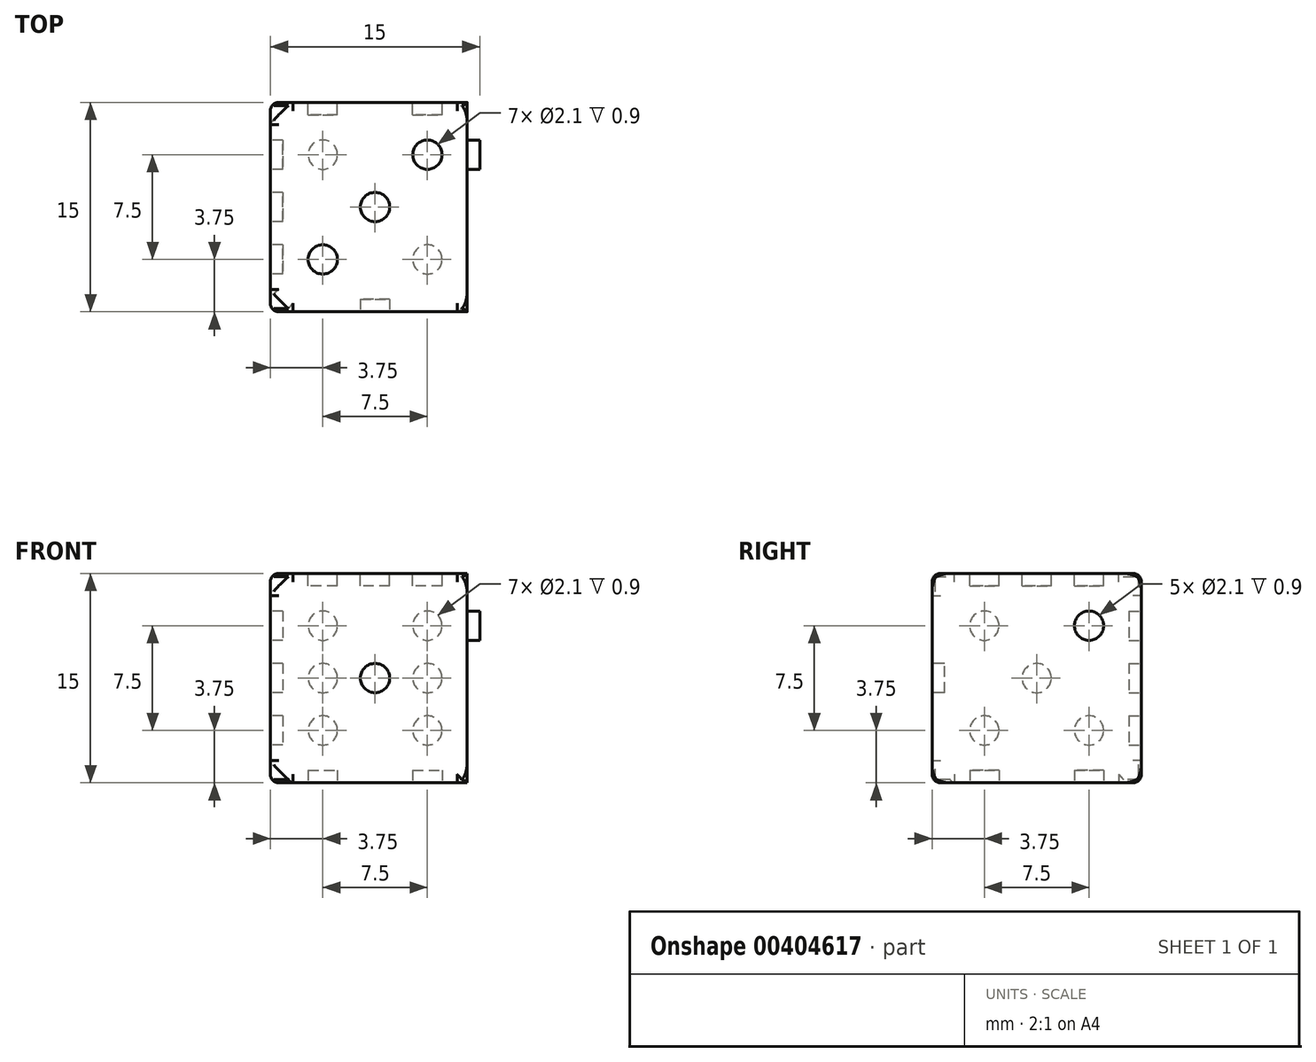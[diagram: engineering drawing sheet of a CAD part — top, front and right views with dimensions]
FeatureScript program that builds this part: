
annotation { "Feature Type Name" : "Feature", "Feature Type Description" : "" }
export const myFeature = defineFeature(function(context is Context, id is Id, definition is map)
    precondition{}
    {
        {
            var Q0;
            Q0=qCreatedBy(makeId("Front.planeOp"),FACE);
            var sketch = newSketch(context, id + "F0", { "sketchPlane" : qUnion([Q0])});
            skLineSegment(sketch, "E0.bottom", {"start": v(0, 25) * mm, "end": v(25, 25) * mm});
            skLineSegment(sketch, "E0.top", {"start": v(0, 0) * mm, "end": v(25, 0) * mm});
            skLineSegment(sketch, "E0.left", {"start": v(0, 25) * mm, "end": v(0, 0) * mm});
            skLineSegment(sketch, "E0.right", {"start": v(25, 25) * mm, "end": v(25, 0) * mm});
            skSolve(sketch);
        }
        {
            var Q0;
            Q0=makeQuery(id+"F0.imprint","IMPRINT",FACE,{"disambiguationData":[TD([[makeQuery(id+"F0.imprint","IMPRINT",EDGE,{"derivedFrom":sQuery(id+"F0.wireOp",EDGE,"E0.bottom")}),-1.0]])]});
            extrude(context, id + "F1", {"entities" : qUnion([Q0]), "oppositeDirection" : true, "depth" : 25 * mm});
        }
        {
            var Q0;
            Q0=makeQuery(id+"F1.opExtrude","CAP_FACE",FACE,{"disambiguationData":[OSD([sQuery(id+"F0.wireOp",EDGE,"E0.bottom"),sQuery(id+"F0.wireOp",EDGE,"E0.top"),sQuery(id+"F0.wireOp",EDGE,"E0.left"),sQuery(id+"F0.wireOp",EDGE,"E0.right")])],"isStart":true});
            var sketch = newSketch(context, id + "F2", { "sketchPlane" : qUnion([Q0])});
            skLineSegment(sketch, "E1", {"start": v(0, 12.5) * mm, "end": v(25, 12.5) * mm, "construction": true});
            skLineSegment(sketch, "E2", {"start": v(12.5, 25) * mm, "end": v(12.5, 0) * mm, "construction": true});
            skCircle(sketch, "E3", {"center": v(12.5, 12.5) * mm, "radius": 1.75 * mm});
            skSolve(sketch);
        }
        {
            var Q0;
            Q0 = qSketchRegion(id + "F2", true);
            extrude(context, id + "F3", {"entities" : qUnion([Q0]), "operationType" : NewBodyOperationType.REMOVE, "oppositeDirection" : true, "depth" : 1.5 * mm});
        }
        {
            var Q0;
            Q0=makeQuery(id+"F1.opExtrude","SWEPT_FACE",FACE,{"disambiguationData":[OSD([sQuery(id+"F0.wireOp",EDGE,"E0.right")])]});
            var sketch = newSketch(context, id + "F4", { "sketchPlane" : qUnion([Q0])});
            skLineSegment(sketch, "E4", {"start": v(0, 0) * mm, "end": v(25, 25) * mm, "construction": true});
            skCircle(sketch, "E5", {"center": v(6.25, 6.25) * mm, "radius": 1.75 * mm});
            skLineSegment(sketch, "E6", {"start": v(0, 25) * mm, "end": v(25, 0) * mm, "construction": true});
            skCircle(sketch, "E7.MirrorC", {"center": v(18.75, 18.75) * mm, "radius": 1.75 * mm});
            skLineSegment(sketch, "E8", {"start": v(12.5, 12.5) * mm, "end": v(12.5, 0) * mm, "construction": true});
            skLineSegment(sketch, "E9", {"start": v(12.5, 0) * mm, "end": v(6.25, 6.25) * mm, "construction": true});
            skSolve(sketch);
        }
        {
            var Q0;
            Q0=makeQuery(id+"F4.imprint","IMPRINT",FACE,{"disambiguationData":[TD([[makeQuery(id+"F4.imprint","IMPRINT",EDGE,{"derivedFrom":sQuery(id+"F4.wireOp",EDGE,"E7.MirrorC")}),-1.0]])]});
            var Q1;
            Q1=makeQuery(id+"F4.imprint","IMPRINT",FACE,{"disambiguationData":[TD([[makeQuery(id+"F4.imprint","IMPRINT",EDGE,{"derivedFrom":sQuery(id+"F4.wireOp",EDGE,"E5")}),1.0]])]});
            var Q2;
            Q2=sQuery(id+"F4.wireOp",EDGE,"E5");
            var Q3;
            Q3=sQuery(id+"F4.wireOp",EDGE,"E7.MirrorC");
            extrude(context, id + "F5", {"entities" : qUnion([Q0, Q1]), "operationType" : NewBodyOperationType.REMOVE, "surfaceEntities" : qUnion([Q2, Q3]), "oppositeDirection" : true, "depth" : 1.5 * mm});
        }
        {
            var Q0;
            Q0=makeQuery(id+"F1.opExtrude","CAP_FACE",FACE,{"disambiguationData":[OSD([sQuery(id+"F0.wireOp",EDGE,"E0.bottom"),sQuery(id+"F0.wireOp",EDGE,"E0.top"),sQuery(id+"F0.wireOp",EDGE,"E0.left"),sQuery(id+"F0.wireOp",EDGE,"E0.right")])],"isStart":false});
            var sketch = newSketch(context, id + "F6", { "sketchPlane" : qUnion([Q0])});
            skLineSegment(sketch, "E10", {"start": v(-12.5, 25) * mm, "end": v(-12.5, 0) * mm, "construction": true});
            skLineSegment(sketch, "E11", {"start": v(-25, 25) * mm, "end": v(0, 0) * mm, "construction": true});
            skLineSegment(sketch, "E12", {"start": v(0, 25) * mm, "end": v(-25, 0) * mm, "construction": true});
            skLineSegment(sketch, "E13", {"start": v(0, 12.5) * mm, "end": v(-25, 12.5) * mm, "construction": true});
            skLineSegment(sketch, "E14", {"start": v(-25, 12.5) * mm, "end": v(-18.75, 18.75) * mm, "construction": true});
            skLineSegment(sketch, "E15", {"start": v(-18.75, 25) * mm, "end": v(-18.75, 0) * mm, "construction": true});
            skLineSegment(sketch, "E16", {"start": v(0, 12.5) * mm, "end": v(-6.25, 18.75) * mm, "construction": true});
            skLineSegment(sketch, "E17", {"start": v(-6.25, 25) * mm, "end": v(-6.25, 0) * mm, "construction": true});
            skCircle(sketch, "E18", {"center": v(-18.75, 18.75) * mm, "radius": 1.75 * mm});
            skCircle(sketch, "E19", {"center": v(-18.75, 12.5) * mm, "radius": 1.75 * mm});
            skCircle(sketch, "E20", {"center": v(-18.75, 6.25) * mm, "radius": 1.75 * mm});
            skCircle(sketch, "E21", {"center": v(-6.25, 18.75) * mm, "radius": 1.75 * mm});
            skCircle(sketch, "E22", {"center": v(-6.25, 12.5) * mm, "radius": 1.75 * mm});
            skCircle(sketch, "E23", {"center": v(-6.25, 6.25) * mm, "radius": 1.75 * mm});
            skSolve(sketch);
        }
        {
            var Q0;
            Q0 = qSketchRegion(id + "F6", true);
            extrude(context, id + "F7", {"entities" : qUnion([Q0]), "operationType" : NewBodyOperationType.REMOVE, "oppositeDirection" : true, "depth" : 1.5 * mm});
        }
        {
            var Q0;
            Q0=makeQuery(id+"F1.opExtrude","SWEPT_FACE",FACE,{"disambiguationData":[OSD([sQuery(id+"F0.wireOp",EDGE,"E0.left")])]});
            var sketch = newSketch(context, id + "F8", { "sketchPlane" : qUnion([Q0])});
            skLineSegment(sketch, "E24", {"start": v(-12.5, 25) * mm, "end": v(-12.5, 0) * mm, "construction": true});
            skLineSegment(sketch, "E25", {"start": v(0, 12.5) * mm, "end": v(-25, 12.5) * mm, "construction": true});
            skLineSegment(sketch, "E26", {"start": v(-25, 12.5) * mm, "end": v(-12.5, 25) * mm, "construction": true});
            skLineSegment(sketch, "E27", {"start": v(-12.5, 12.5) * mm, "end": v(-25, 25) * mm, "construction": true});
            skLineSegment(sketch, "E28", {"start": v(-18.75, 18.75) * mm, "end": v(-18.75, 12.5) * mm, "construction": true});
            skLineSegment(sketch, "E29", {"start": v(-18.75, 18.75) * mm, "end": v(-12.5, 18.75) * mm, "construction": true});
            skCircle(sketch, "E30", {"center": v(-18.75, 18.75) * mm, "radius": 1.75 * mm});
            skCircle(sketch, "E31.MirrorC", {"center": v(-18.75, 6.25) * mm, "radius": 1.75 * mm});
            skLineSegment(sketch, "E32.MirrorCS", {"start": v(-12.5, 0) * mm, "end": v(-12.5, 25) * mm, "construction": true});
            skCircle(sketch, "E33.MirrorC", {"center": v(-6.25, 18.75) * mm, "radius": 1.75 * mm});
            skCircle(sketch, "E34.MirrorC", {"center": v(-6.25, 6.25) * mm, "radius": 1.75 * mm});
            skCircle(sketch, "E35", {"center": v(-12.5, 12.5) * mm, "radius": 1.75 * mm});
            skSolve(sketch);
        }
        {
            var Q0;
            Q0 = qSketchRegion(id + "F8", true);
            extrude(context, id + "F9", {"entities" : qUnion([Q0]), "operationType" : NewBodyOperationType.REMOVE, "oppositeDirection" : true, "depth" : 1.5 * mm});
        }
        {
            var Q0;
            Q0=makeQuery(id+"F1.opExtrude","SWEPT_FACE",FACE,{"disambiguationData":[OSD([sQuery(id+"F0.wireOp",EDGE,"E0.bottom")])]});
            var sketch = newSketch(context, id + "F10", { "sketchPlane" : qUnion([Q0])});
            skLineSegment(sketch, "E36", {"start": v(0, 0) * mm, "end": v(25, 25) * mm, "construction": true});
            skLineSegment(sketch, "E37", {"start": v(25, 25) * mm, "end": v(0, 25) * mm, "construction": true});
            skLineSegment(sketch, "E38", {"start": v(0, 25) * mm, "end": v(25, 0) * mm, "construction": true});
            skLineSegment(sketch, "E39", {"start": v(12.5, 12.5) * mm, "end": v(0, 12.5) * mm, "construction": true});
            skLineSegment(sketch, "E40", {"start": v(0, 12.5) * mm, "end": v(6.25, 6.25) * mm, "construction": true});
            skCircle(sketch, "E41", {"center": v(6.25, 6.25) * mm, "radius": 1.75 * mm});
            skCircle(sketch, "E42.MirrorC", {"center": v(18.75, 18.75) * mm, "radius": 1.75 * mm});
            skCircle(sketch, "E43", {"center": v(12.5, 12.5) * mm, "radius": 1.75 * mm});
            skSolve(sketch);
        }
        {
            var Q0;
            Q0 = qSketchRegion(id + "F10", true);
            extrude(context, id + "F11", {"entities" : qUnion([Q0]), "operationType" : NewBodyOperationType.REMOVE, "oppositeDirection" : true, "depth" : 1.5 * mm});
        }
        {
            var Q0;
            Q0=makeQuery(id+"F1.opExtrude","SWEPT_FACE",FACE,{"disambiguationData":[OSD([sQuery(id+"F0.wireOp",EDGE,"E0.top")])]});
            var sketch = newSketch(context, id + "F12", { "sketchPlane" : qUnion([Q0])});
            skLineSegment(sketch, "E44", {"start": v(12.5, 0) * mm, "end": v(12.5, -25) * mm, "construction": true});
            skLineSegment(sketch, "E45", {"start": v(12.5, -25) * mm, "end": v(0, -12.5) * mm, "construction": true});
            skLineSegment(sketch, "E46", {"start": v(0, -12.5) * mm, "end": v(25, -12.5) * mm, "construction": true});
            skLineSegment(sketch, "E47", {"start": v(0, -25) * mm, "end": v(6.25, -18.75) * mm, "construction": true});
            skLineSegment(sketch, "E48", {"start": v(6.25, -25) * mm, "end": v(6.25, 0) * mm, "construction": true});
            skCircle(sketch, "E49", {"center": v(6.25, -18.75) * mm, "radius": 1.75 * mm});
            skCircle(sketch, "E50.MirrorC", {"center": v(6.25, -6.25) * mm, "radius": 1.75 * mm});
            skCircle(sketch, "E51.MirrorC", {"center": v(18.75, -18.75) * mm, "radius": 1.75 * mm});
            skCircle(sketch, "E52.MirrorC", {"center": v(18.75, -6.25) * mm, "radius": 1.75 * mm});
            skSolve(sketch);
        }
        {
            var Q0;
            Q0 = qSketchRegion(id + "F12", true);
            extrude(context, id + "F13", {"entities" : qUnion([Q0]), "operationType" : NewBodyOperationType.REMOVE, "oppositeDirection" : true, "depth" : 1.5 * mm});
        }
        {
            var Q0;
            Q0=makeQuery(id+"F1.opExtrude","SWEPT_BODY",BODY,{"disambiguationData":[OSD([sQuery(id+"F0.wireOp",EDGE,"E0.bottom"),sQuery(id+"F0.wireOp",EDGE,"E0.top"),sQuery(id+"F0.wireOp",EDGE,"E0.left"),sQuery(id+"F0.wireOp",EDGE,"E0.right")])]});
            transform(context, id + "F14", {"entities" : qUnion([Q0]), "transformType" : TransformType.TRANSLATION_3D, "dx" : (-25 / 2) * mm, "dy" : (-25 / 2) * mm, "dz" : (-25 / 2) * mm, "makeCopy" : false});
        }
        {
            var Q0;
            Q0=qCreatedBy(makeId("Front.planeOp"),FACE);
            var sketch = newSketch(context, id + "F15", { "sketchPlane" : qUnion([Q0])});
            skArc(sketch, "E53", {"start": v(20, 0) * mm, "mid": v(0, 20) * mm, "end": v(-20, 0) * mm});
            skLineSegment(sketch, "E54", {"start": v(20, 0) * mm, "end": v(-20, 0) * mm});
            skSolve(sketch);
        }
        {
            var Q0;
            Q0=makeQuery(id+"F15.imprint","IMPRINT",FACE,{"disambiguationData":[TD([[makeQuery(id+"F15.imprint","IMPRINT",EDGE,{"derivedFrom":sQuery(id+"F15.wireOp",EDGE,"E53")}),1.0]])]});
            var Q1;
            Q1=sQuery(id+"F15.wireOp",EDGE,"E54");
            revolve(context, id + "F16", {"entities" : qUnion([Q0]), "axis" : qUnion([Q1]), "revolveType" : RevolveType.FULL});
        }
        {
            var Q0;
            Q0=makeQuery(id+"F1.opExtrude","CAP_EDGE",EDGE,{"disambiguationData":[OSD([sQuery(id+"F0.wireOp",EDGE,"E0.left")])],"isStart":false});
            var Q1;
            Q1=makeQuery(id+"F1.opExtrude","CAP_EDGE",EDGE,{"disambiguationData":[OSD([sQuery(id+"F0.wireOp",EDGE,"E0.top")])],"isStart":false});
            var Q2;
            Q2=makeQuery(id+"F1.opExtrude","SWEPT_EDGE",EDGE,{"disambiguationData":[OSD([sQuery(id+"F0.wireOp",EDGE,"E0.top"),sQuery(id+"F0.wireOp",EDGE,"E0.left")])]});
            var Q3;
            Q3=makeQuery(id+"F1.opExtrude","CAP_EDGE",EDGE,{"disambiguationData":[OSD([sQuery(id+"F0.wireOp",EDGE,"E0.left")])],"isStart":true});
            var Q4;
            Q4=makeQuery(id+"F1.opExtrude","SWEPT_EDGE",EDGE,{"disambiguationData":[OSD([sQuery(id+"F0.wireOp",EDGE,"E0.bottom"),sQuery(id+"F0.wireOp",EDGE,"E0.left")])]});
            var Q5;
            Q5=makeQuery(id+"F1.opExtrude","CAP_EDGE",EDGE,{"disambiguationData":[OSD([sQuery(id+"F0.wireOp",EDGE,"E0.right")])],"isStart":false});
            var Q6;
            Q6=makeQuery(id+"F1.opExtrude","SWEPT_EDGE",EDGE,{"disambiguationData":[OSD([sQuery(id+"F0.wireOp",EDGE,"E0.top"),sQuery(id+"F0.wireOp",EDGE,"E0.right")])]});
            var Q7;
            Q7=makeQuery(id+"F1.opExtrude","CAP_EDGE",EDGE,{"disambiguationData":[OSD([sQuery(id+"F0.wireOp",EDGE,"E0.top")])],"isStart":true});
            var Q8;
            Q8=makeQuery(id+"F1.opExtrude","CAP_EDGE",EDGE,{"disambiguationData":[OSD([sQuery(id+"F0.wireOp",EDGE,"E0.bottom")])],"isStart":false});
            var Q9;
            Q9=makeQuery(id+"F1.opExtrude","CAP_EDGE",EDGE,{"disambiguationData":[OSD([sQuery(id+"F0.wireOp",EDGE,"E0.bottom")])],"isStart":true});
            var Q10;
            Q10=makeQuery(id+"F1.opExtrude","CAP_EDGE",EDGE,{"disambiguationData":[OSD([sQuery(id+"F0.wireOp",EDGE,"E0.right")])],"isStart":true});
            var Q11;
            Q11=makeQuery(id+"F1.opExtrude","SWEPT_EDGE",EDGE,{"disambiguationData":[OSD([sQuery(id+"F0.wireOp",EDGE,"E0.bottom"),sQuery(id+"F0.wireOp",EDGE,"E0.right")])]});
            fillet(context, id + "F17", {"entities" : qUnion([Q0, Q1, Q2, Q3, Q4, Q5, Q6, Q7, Q8, Q9, Q10, Q11]), "radius" : 1 * mm, "tangentPropagation" : true, "allowEdgeOverflow" : false});
        }
        {
            var Q0;
            Q0=makeQuery(id+"F16.opRevolve","SWEPT_BODY",BODY,{"disambiguationData":[OSD([sQuery(id+"F15.wireOp",EDGE,"E53"),sQuery(id+"F15.wireOp",EDGE,"E54")])]});
            var Q1;
            Q1=makeQuery(id+"F1.opExtrude","SWEPT_BODY",BODY,{"disambiguationData":[OSD([sQuery(id+"F0.wireOp",EDGE,"E0.bottom"),sQuery(id+"F0.wireOp",EDGE,"E0.top"),sQuery(id+"F0.wireOp",EDGE,"E0.left"),sQuery(id+"F0.wireOp",EDGE,"E0.right")])]});
            booleanBodies(context, id + "F18", {"operationType" : BooleanOperationType.INTERSECTION, "tools" : qUnion([Q0, Q1])});
        }
        {
            var Q0;
            {var subQ0=sQuery(id+"F0.wireOp",EDGE,"E0.right");var subQ1=sQuery(id+"F0.wireOp",EDGE,"E0.bottom");Q0=makeQuery(id+"F18.opBoolean","SPLIT",FACE,{"disambiguationData":[TD([makeQuery(id+"F1.opExtrude","SWEPT_FACE",FACE,{"disambiguationData":[OSD([subQ1])]}),makeQuery(id+"F1.opExtrude","CAP_FACE",FACE,{"disambiguationData":[OSD([subQ1,sQuery(id+"F0.wireOp",EDGE,"E0.top"),sQuery(id+"F0.wireOp",EDGE,"E0.left"),subQ0])],"isStart":true}),makeQuery(id+"F1.opExtrude","SWEPT_FACE",FACE,{"disambiguationData":[OSD([subQ0])]}),makeQuery(id+"F17.opFillet","BLEND_FACE",FACE,{"disambiguationData":[OSD([subQ1,subQ0]),TDD([makeQuery(id+"F1.opExtrude","SWEPT_EDGE",EDGE,{"disambiguationData":[OSD([subQ1,subQ0])]})])]}),makeQuery(id+"F17.opFillet","BLEND_FACE",FACE,{"disambiguationData":[OSD([subQ1]),TDD([makeQuery(id+"F1.opExtrude","CAP_EDGE",EDGE,{"disambiguationData":[OSD([subQ1])],"isStart":true})])]}),makeQuery(id+"F17.opFillet","BLEND_FACE",FACE,{"disambiguationData":[OSD([subQ0]),TDD([makeQuery(id+"F1.opExtrude","CAP_EDGE",EDGE,{"disambiguationData":[OSD([subQ0])],"isStart":true})])]})])],"derivedFrom":makeQuery(id+"F16.opRevolve","SWEPT_FACE",FACE,{"disambiguationData":[OSD([sQuery(id+"F15.wireOp",EDGE,"E53")])]})});}
            var Q1;
            {var subQ0=sQuery(id+"F0.wireOp",EDGE,"E0.left");var subQ1=sQuery(id+"F0.wireOp",EDGE,"E0.bottom");Q1=makeQuery(id+"F18.opBoolean","SPLIT",FACE,{"disambiguationData":[TD([makeQuery(id+"F1.opExtrude","SWEPT_FACE",FACE,{"disambiguationData":[OSD([subQ1])]}),makeQuery(id+"F1.opExtrude","CAP_FACE",FACE,{"disambiguationData":[OSD([subQ1,sQuery(id+"F0.wireOp",EDGE,"E0.top"),subQ0,sQuery(id+"F0.wireOp",EDGE,"E0.right")])],"isStart":true}),makeQuery(id+"F1.opExtrude","SWEPT_FACE",FACE,{"disambiguationData":[OSD([subQ0])]}),makeQuery(id+"F17.opFillet","BLEND_FACE",FACE,{"disambiguationData":[OSD([subQ1,subQ0]),TDD([makeQuery(id+"F1.opExtrude","SWEPT_EDGE",EDGE,{"disambiguationData":[OSD([subQ1,subQ0])]})])]}),makeQuery(id+"F17.opFillet","BLEND_FACE",FACE,{"disambiguationData":[OSD([subQ1]),TDD([makeQuery(id+"F1.opExtrude","CAP_EDGE",EDGE,{"disambiguationData":[OSD([subQ1])],"isStart":true})])]}),makeQuery(id+"F17.opFillet","BLEND_FACE",FACE,{"disambiguationData":[OSD([subQ0]),TDD([makeQuery(id+"F1.opExtrude","CAP_EDGE",EDGE,{"disambiguationData":[OSD([subQ0])],"isStart":true})])]})])],"derivedFrom":makeQuery(id+"F16.opRevolve","SWEPT_FACE",FACE,{"disambiguationData":[OSD([sQuery(id+"F15.wireOp",EDGE,"E53")])]})});}
            var Q2;
            {var subQ0=sQuery(id+"F0.wireOp",EDGE,"E0.right");var subQ1=sQuery(id+"F0.wireOp",EDGE,"E0.bottom");Q2=makeQuery(id+"F18.opBoolean","SPLIT",FACE,{"disambiguationData":[TD([makeQuery(id+"F1.opExtrude","SWEPT_FACE",FACE,{"disambiguationData":[OSD([subQ1])]}),makeQuery(id+"F1.opExtrude","CAP_FACE",FACE,{"disambiguationData":[OSD([subQ1,sQuery(id+"F0.wireOp",EDGE,"E0.top"),sQuery(id+"F0.wireOp",EDGE,"E0.left"),subQ0])],"isStart":false}),makeQuery(id+"F1.opExtrude","SWEPT_FACE",FACE,{"disambiguationData":[OSD([subQ0])]}),makeQuery(id+"F17.opFillet","BLEND_FACE",FACE,{"disambiguationData":[OSD([subQ1,subQ0]),TDD([makeQuery(id+"F1.opExtrude","SWEPT_EDGE",EDGE,{"disambiguationData":[OSD([subQ1,subQ0])]})])]}),makeQuery(id+"F17.opFillet","BLEND_FACE",FACE,{"disambiguationData":[OSD([subQ1]),TDD([makeQuery(id+"F1.opExtrude","CAP_EDGE",EDGE,{"disambiguationData":[OSD([subQ1])],"isStart":false})])]}),makeQuery(id+"F17.opFillet","BLEND_FACE",FACE,{"disambiguationData":[OSD([subQ0]),TDD([makeQuery(id+"F1.opExtrude","CAP_EDGE",EDGE,{"disambiguationData":[OSD([subQ0])],"isStart":false})])]})])],"derivedFrom":makeQuery(id+"F16.opRevolve","SWEPT_FACE",FACE,{"disambiguationData":[OSD([sQuery(id+"F15.wireOp",EDGE,"E53")])]})});}
            var Q3;
            {var subQ0=sQuery(id+"F0.wireOp",EDGE,"E0.left");var subQ1=sQuery(id+"F0.wireOp",EDGE,"E0.bottom");Q3=makeQuery(id+"F18.opBoolean","SPLIT",FACE,{"disambiguationData":[TD([makeQuery(id+"F1.opExtrude","SWEPT_FACE",FACE,{"disambiguationData":[OSD([subQ1])]}),makeQuery(id+"F1.opExtrude","CAP_FACE",FACE,{"disambiguationData":[OSD([subQ1,sQuery(id+"F0.wireOp",EDGE,"E0.top"),subQ0,sQuery(id+"F0.wireOp",EDGE,"E0.right")])],"isStart":false}),makeQuery(id+"F1.opExtrude","SWEPT_FACE",FACE,{"disambiguationData":[OSD([subQ0])]}),makeQuery(id+"F17.opFillet","BLEND_FACE",FACE,{"disambiguationData":[OSD([subQ1,subQ0]),TDD([makeQuery(id+"F1.opExtrude","SWEPT_EDGE",EDGE,{"disambiguationData":[OSD([subQ1,subQ0])]})])]}),makeQuery(id+"F17.opFillet","BLEND_FACE",FACE,{"disambiguationData":[OSD([subQ1]),TDD([makeQuery(id+"F1.opExtrude","CAP_EDGE",EDGE,{"disambiguationData":[OSD([subQ1])],"isStart":false})])]}),makeQuery(id+"F17.opFillet","BLEND_FACE",FACE,{"disambiguationData":[OSD([subQ0]),TDD([makeQuery(id+"F1.opExtrude","CAP_EDGE",EDGE,{"disambiguationData":[OSD([subQ0])],"isStart":false})])]})])],"derivedFrom":makeQuery(id+"F16.opRevolve","SWEPT_FACE",FACE,{"disambiguationData":[OSD([sQuery(id+"F15.wireOp",EDGE,"E53")])]})});}
            var Q4;
            {var subQ0=sQuery(id+"F0.wireOp",EDGE,"E0.left");var subQ1=sQuery(id+"F0.wireOp",EDGE,"E0.top");Q4=makeQuery(id+"F18.opBoolean","SPLIT",FACE,{"disambiguationData":[TD([makeQuery(id+"F1.opExtrude","CAP_FACE",FACE,{"disambiguationData":[OSD([sQuery(id+"F0.wireOp",EDGE,"E0.bottom"),subQ1,subQ0,sQuery(id+"F0.wireOp",EDGE,"E0.right")])],"isStart":true}),makeQuery(id+"F1.opExtrude","SWEPT_FACE",FACE,{"disambiguationData":[OSD([subQ1])]}),makeQuery(id+"F1.opExtrude","SWEPT_FACE",FACE,{"disambiguationData":[OSD([subQ0])]}),makeQuery(id+"F17.opFillet","BLEND_FACE",FACE,{"disambiguationData":[OSD([subQ1,subQ0]),TDD([makeQuery(id+"F1.opExtrude","SWEPT_EDGE",EDGE,{"disambiguationData":[OSD([subQ1,subQ0])]})])]}),makeQuery(id+"F17.opFillet","BLEND_FACE",FACE,{"disambiguationData":[OSD([subQ1]),TDD([makeQuery(id+"F1.opExtrude","CAP_EDGE",EDGE,{"disambiguationData":[OSD([subQ1])],"isStart":true})])]}),makeQuery(id+"F17.opFillet","BLEND_FACE",FACE,{"disambiguationData":[OSD([subQ0]),TDD([makeQuery(id+"F1.opExtrude","CAP_EDGE",EDGE,{"disambiguationData":[OSD([subQ0])],"isStart":true})])]})])],"derivedFrom":makeQuery(id+"F16.opRevolve","SWEPT_FACE",FACE,{"disambiguationData":[OSD([sQuery(id+"F15.wireOp",EDGE,"E53")])]})});}
            var Q5;
            {var subQ0=sQuery(id+"F0.wireOp",EDGE,"E0.left");var subQ1=sQuery(id+"F0.wireOp",EDGE,"E0.top");Q5=makeQuery(id+"F18.opBoolean","SPLIT",FACE,{"disambiguationData":[TD([makeQuery(id+"F1.opExtrude","CAP_FACE",FACE,{"disambiguationData":[OSD([sQuery(id+"F0.wireOp",EDGE,"E0.bottom"),subQ1,subQ0,sQuery(id+"F0.wireOp",EDGE,"E0.right")])],"isStart":false}),makeQuery(id+"F1.opExtrude","SWEPT_FACE",FACE,{"disambiguationData":[OSD([subQ1])]}),makeQuery(id+"F1.opExtrude","SWEPT_FACE",FACE,{"disambiguationData":[OSD([subQ0])]}),makeQuery(id+"F17.opFillet","BLEND_FACE",FACE,{"disambiguationData":[OSD([subQ1,subQ0]),TDD([makeQuery(id+"F1.opExtrude","SWEPT_EDGE",EDGE,{"disambiguationData":[OSD([subQ1,subQ0])]})])]}),makeQuery(id+"F17.opFillet","BLEND_FACE",FACE,{"disambiguationData":[OSD([subQ1]),TDD([makeQuery(id+"F1.opExtrude","CAP_EDGE",EDGE,{"disambiguationData":[OSD([subQ1])],"isStart":false})])]}),makeQuery(id+"F17.opFillet","BLEND_FACE",FACE,{"disambiguationData":[OSD([subQ0]),TDD([makeQuery(id+"F1.opExtrude","CAP_EDGE",EDGE,{"disambiguationData":[OSD([subQ0])],"isStart":false})])]})])],"derivedFrom":makeQuery(id+"F16.opRevolve","SWEPT_FACE",FACE,{"disambiguationData":[OSD([sQuery(id+"F15.wireOp",EDGE,"E53")])]})});}
            var Q6;
            {var subQ0=sQuery(id+"F0.wireOp",EDGE,"E0.right");var subQ1=sQuery(id+"F0.wireOp",EDGE,"E0.top");Q6=makeQuery(id+"F18.opBoolean","SPLIT",FACE,{"disambiguationData":[TD([makeQuery(id+"F1.opExtrude","CAP_FACE",FACE,{"disambiguationData":[OSD([sQuery(id+"F0.wireOp",EDGE,"E0.bottom"),subQ1,sQuery(id+"F0.wireOp",EDGE,"E0.left"),subQ0])],"isStart":false}),makeQuery(id+"F1.opExtrude","SWEPT_FACE",FACE,{"disambiguationData":[OSD([subQ1])]}),makeQuery(id+"F1.opExtrude","SWEPT_FACE",FACE,{"disambiguationData":[OSD([subQ0])]}),makeQuery(id+"F17.opFillet","BLEND_FACE",FACE,{"disambiguationData":[OSD([subQ1,subQ0]),TDD([makeQuery(id+"F1.opExtrude","SWEPT_EDGE",EDGE,{"disambiguationData":[OSD([subQ1,subQ0])]})])]}),makeQuery(id+"F17.opFillet","BLEND_FACE",FACE,{"disambiguationData":[OSD([subQ1]),TDD([makeQuery(id+"F1.opExtrude","CAP_EDGE",EDGE,{"disambiguationData":[OSD([subQ1])],"isStart":false})])]}),makeQuery(id+"F17.opFillet","BLEND_FACE",FACE,{"disambiguationData":[OSD([subQ0]),TDD([makeQuery(id+"F1.opExtrude","CAP_EDGE",EDGE,{"disambiguationData":[OSD([subQ0])],"isStart":false})])]})])],"derivedFrom":makeQuery(id+"F16.opRevolve","SWEPT_FACE",FACE,{"disambiguationData":[OSD([sQuery(id+"F15.wireOp",EDGE,"E53")])]})});}
            var Q7;
            {var subQ0=sQuery(id+"F0.wireOp",EDGE,"E0.right");var subQ1=sQuery(id+"F0.wireOp",EDGE,"E0.top");Q7=makeQuery(id+"F18.opBoolean","SPLIT",FACE,{"disambiguationData":[TD([makeQuery(id+"F1.opExtrude","CAP_FACE",FACE,{"disambiguationData":[OSD([sQuery(id+"F0.wireOp",EDGE,"E0.bottom"),subQ1,sQuery(id+"F0.wireOp",EDGE,"E0.left"),subQ0])],"isStart":true}),makeQuery(id+"F1.opExtrude","SWEPT_FACE",FACE,{"disambiguationData":[OSD([subQ1])]}),makeQuery(id+"F1.opExtrude","SWEPT_FACE",FACE,{"disambiguationData":[OSD([subQ0])]}),makeQuery(id+"F17.opFillet","BLEND_FACE",FACE,{"disambiguationData":[OSD([subQ1,subQ0]),TDD([makeQuery(id+"F1.opExtrude","SWEPT_EDGE",EDGE,{"disambiguationData":[OSD([subQ1,subQ0])]})])]}),makeQuery(id+"F17.opFillet","BLEND_FACE",FACE,{"disambiguationData":[OSD([subQ1]),TDD([makeQuery(id+"F1.opExtrude","CAP_EDGE",EDGE,{"disambiguationData":[OSD([subQ1])],"isStart":true})])]}),makeQuery(id+"F17.opFillet","BLEND_FACE",FACE,{"disambiguationData":[OSD([subQ0]),TDD([makeQuery(id+"F1.opExtrude","CAP_EDGE",EDGE,{"disambiguationData":[OSD([subQ0])],"isStart":true})])]})])],"derivedFrom":makeQuery(id+"F16.opRevolve","SWEPT_FACE",FACE,{"disambiguationData":[OSD([sQuery(id+"F15.wireOp",EDGE,"E53")])]})});}
            fillet(context, id + "F19", {"entities" : qUnion([Q0, Q1, Q2, Q3, Q4, Q5, Q6, Q7]), "radius" : 1 * mm, "tangentPropagation" : true, "allowEdgeOverflow" : false});
        }
        {
            var Q0;
            Q0=makeQuery(id+"F18.opBoolean","INTERSECT",BODY,{"derivedFrom":[makeQuery(id+"F1.opExtrude","SWEPT_BODY",BODY,{"disambiguationData":[OSD([sQuery(id+"F0.wireOp",EDGE,"E0.bottom"),sQuery(id+"F0.wireOp",EDGE,"E0.top"),sQuery(id+"F0.wireOp",EDGE,"E0.left"),sQuery(id+"F0.wireOp",EDGE,"E0.right")])]}),makeQuery(id+"F16.opRevolve","SWEPT_BODY",BODY,{"disambiguationData":[OSD([sQuery(id+"F15.wireOp",EDGE,"E53"),sQuery(id+"F15.wireOp",EDGE,"E54")])]})]});
            var Q1;
            Q1=qCreatedBy(makeId("Origin.pointOp"),VERTEX);
            transform(context, id + "F20", {"entities" : qUnion([Q0]), "transformType" : TransformType.SCALE_UNIFORMLY, "scale" : 0.6, "scalePoint" : qUnion([Q1]), "makeCopy" : false});
        }
    });
